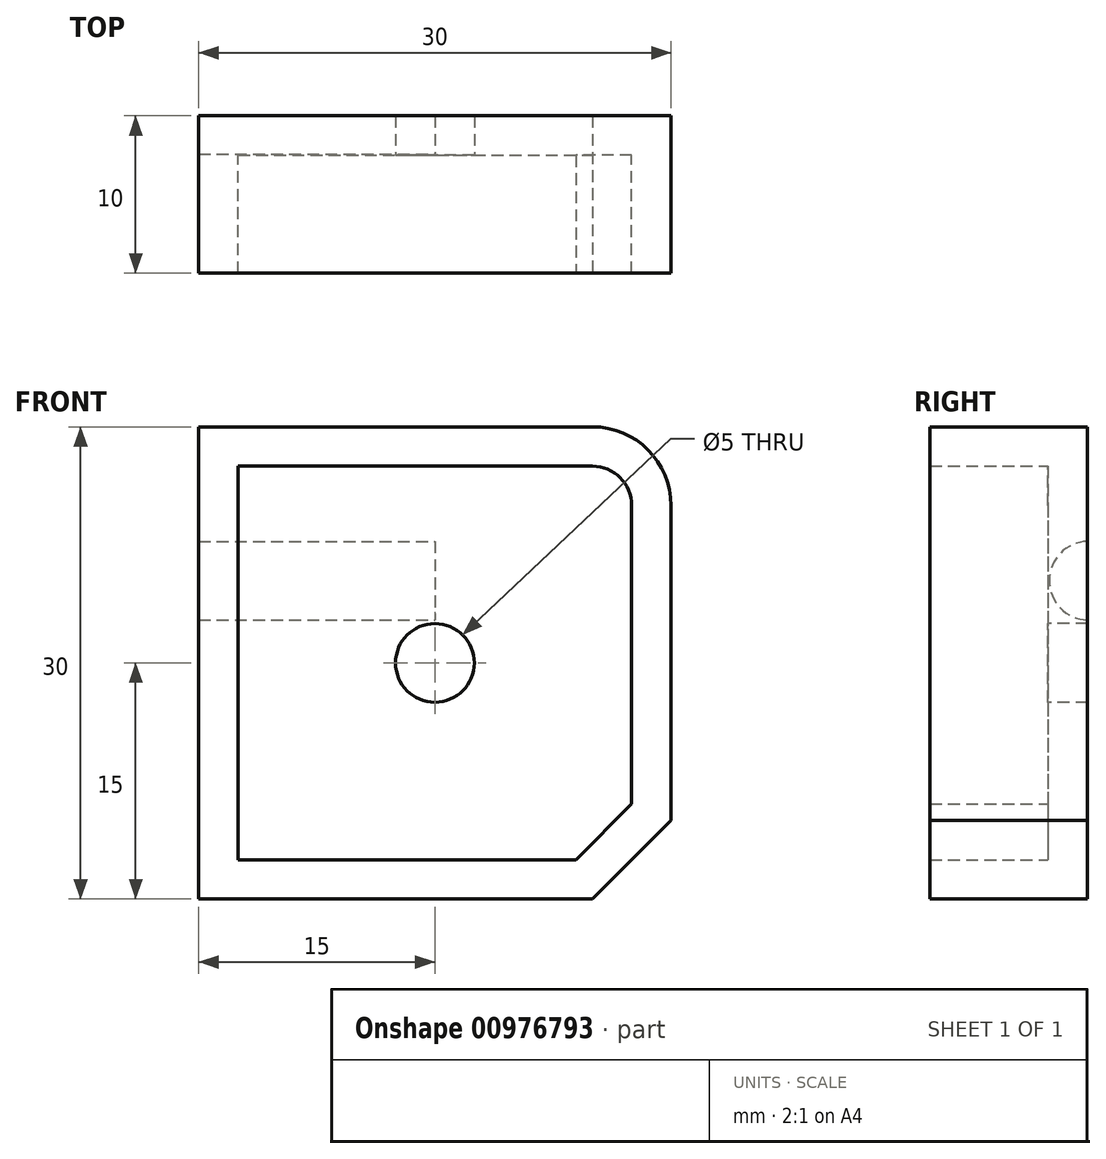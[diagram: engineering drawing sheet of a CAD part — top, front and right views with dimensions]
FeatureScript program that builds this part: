
annotation { "Feature Type Name" : "Feature", "Feature Type Description" : "" }
export const myFeature = defineFeature(function(context is Context, id is Id, definition is map)
    precondition{}
    {
        {
            var Q0;
            Q0=qCreatedBy(makeId("Front.planeOp"),FACE);
            var sketch = newSketch(context, id + "F0", { "sketchPlane" : qUnion([Q0])});
            skLineSegment(sketch, "E0.bottom", {"start": v(-15, 15) * mm, "end": v(15, 15) * mm});
            skLineSegment(sketch, "E0.top", {"start": v(-15, -15) * mm, "end": v(15, -15) * mm});
            skLineSegment(sketch, "E0.left", {"start": v(-15, 15) * mm, "end": v(-15, -15) * mm});
            skLineSegment(sketch, "E0.right", {"start": v(15, 15) * mm, "end": v(15, -15) * mm});
            skPoint(sketch, "E0.middle", {"position": v(0, 0) * mm});
            skSolve(sketch);
        }
        {
            var Q0;
            Q0 = qSketchRegion(id + "F0", true);
            extrude(context, id + "F1", {"entities" : qUnion([Q0]), "endBound" : BoundingType.SYMMETRIC, "depth" : 10 * mm, "offsetDistance" : 25 * mm});
        }
        {
            var Q0;
            Q0=makeQuery(id+"F1.opExtrude","SWEPT_EDGE",EDGE,{"disambiguationData":[OSD([sQuery(id+"F0.wireOp",EDGE,"E0.bottom"),sQuery(id+"F0.wireOp",EDGE,"E0.right")])]});
            fillet(context, id + "F2", {"entities" : qUnion([Q0]), "radius" : 5 * mm, "tangentPropagation" : true, "allowEdgeOverflow" : false});
        }
        {
            var Q0;
            Q0=makeQuery(id+"F1.opExtrude","SWEPT_EDGE",EDGE,{"disambiguationData":[OSD([sQuery(id+"F0.wireOp",EDGE,"E0.top"),sQuery(id+"F0.wireOp",EDGE,"E0.right")])]});
            chamfer(context, id + "F3", {"entities" : qUnion([Q0]), "width" : 5 * mm, "tangentPropagation" : true});
        }
        {
            var Q0;
            Q0=makeQuery(id+"F1.opExtrude","CAP_FACE",FACE,{"disambiguationData":[OSD([sQuery(id+"F0.wireOp",EDGE,"E0.bottom"),sQuery(id+"F0.wireOp",EDGE,"E0.top"),sQuery(id+"F0.wireOp",EDGE,"E0.left"),sQuery(id+"F0.wireOp",EDGE,"E0.right")])],"isStart":false});
            shell(context, id + "F4", {"entities" : qUnion([Q0]), "thickness" : 2.5 * mm});
        }
        {
            var Q0;
            Q0=qCreatedBy(makeId("Front.planeOp"),FACE);
            var sketch = newSketch(context, id + "F5", { "sketchPlane" : qUnion([Q0])});
            skPoint(sketch, "E1", {"position": v(0, 0) * mm});
            skSolve(sketch);
        }
        {
            var Q0;
            Q0=sQuery(id+"F5.wireOp",VERTEX,"E1");
            var Q1;
            Q1=makeQuery(id+"F1.opExtrude","SWEPT_BODY",BODY,{"disambiguationData":[OSD([sQuery(id+"F0.wireOp",EDGE,"E0.bottom"),sQuery(id+"F0.wireOp",EDGE,"E0.top"),sQuery(id+"F0.wireOp",EDGE,"E0.left"),sQuery(id+"F0.wireOp",EDGE,"E0.right")])]});
            hole(context, id + "F6", {"style" : HoleStyle.SIMPLE, "endStyle" : HoleEndStyle.THROUGH, "holeDiameter" : 5 * mm, "majorDiameter" : 5 * mm, "isTappedThrough" : true, "tappedDepth" : 12 * mm, "tapClearance" : 3, "locations" : qUnion([Q0]), "scope" : qUnion([Q1])});
        }
        {
            var Q0;
            Q0=qCreatedBy(makeId("Right.planeOp"),FACE);
            var sketch = newSketch(context, id + "F7", { "sketchPlane" : qUnion([Q0])});
            skPoint(sketch, "E2", {"position": v(5.07, 5.23) * mm});
            skSolve(sketch);
        }
        {
            var Q0;
            Q0=sQuery(id+"F7.wireOp",VERTEX,"E2");
            var Q1;
            Q1=makeQuery(id+"F1.opExtrude","SWEPT_BODY",BODY,{"disambiguationData":[OSD([sQuery(id+"F0.wireOp",EDGE,"E0.bottom"),sQuery(id+"F0.wireOp",EDGE,"E0.top"),sQuery(id+"F0.wireOp",EDGE,"E0.left"),sQuery(id+"F0.wireOp",EDGE,"E0.right")])]});
            hole(context, id + "F8", {"style" : HoleStyle.SIMPLE, "endStyle" : HoleEndStyle.THROUGH, "holeDiameter" : 5 * mm, "majorDiameter" : 5 * mm, "isTappedThrough" : true, "tappedDepth" : 12 * mm, "tapClearance" : 3, "locations" : qUnion([Q0]), "scope" : qUnion([Q1])});
        }
    });
